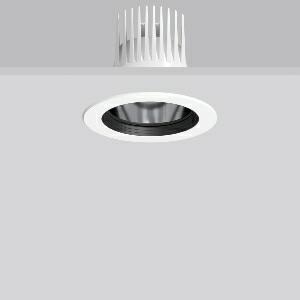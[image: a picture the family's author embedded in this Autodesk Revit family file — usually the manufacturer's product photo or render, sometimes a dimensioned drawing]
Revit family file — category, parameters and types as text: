
# Revit family: heledon_maxi_e_901759_002_2_76_2391
name_source: partatom
category: Lighting Fixtures
units: mm (PartAtom-declared; Revit-internal decimal feet)

## family parameters
Cut with Voids When Loaded = No
Host = Face
Light Source = No
Part Type = Normal
Room Calculation Point = No
Round Connector Dimension = Use Diameter
Shared = No

## types (1)
- HELEDON maxi E (1 x LED Modul 927, 3050 lm, 2700)
    Apparent Load = 25 VA
    Approval mark = CE
    CIE Flux Codes = 97 100 100 100 100
    Color Rendering = 92
    Color Temperature = 2700
    Default Elevation = 1800 mm
    Description = Series: HELEDON maxi
Round recessed downlight. Housing: die-cast aluminium, powder-coated. Black plastic ring and recessed LED to prevent glare from the side. Optical assembly with reflector made of MIRO-Silver with 98% total light reflection for outstanding efficiency - can be changed without tools. Best colour rendering index Ra>90. Suitable for Recessed ceiling mounting. Installation without tools thanks to spring fastening system. Including separate LED converter with connecting cable 600 mm.High quality converter without flickering and stroboscopic effect. Through-wiring box (5 pole) available as accessory. The following accessories can be mounted without use of tools: interchangeable lenses, decorative glasses, honeycomb louvre, clear and frosted diffusers, white interchangeable plastic ring. 
Colour: traffic white, matt (RAL 9016)
Diameter: 162 mm
Height: 3 mm
Cut-out diameter: 152 mm
Recess height: 200 mm
Luminaire: recess height: 135 mm
Lamp: LED
Socket: without socket
Colour temperature: 2700K
Colour rendering index (CRI): 92
System power: 25 W
Rated luminous flux: 3050 lm
Luminous efficiency: 122 lm/W
Control gear: Converter, dimmable, DALI
Protection class: II
Type of protection: IP 20
    Height = 0 mm  [stored 0 ft]
    Lamp = 1 x LED Modul 927
    Lamp Light Flux = 3050 lm
    Lamp count = 1
    Length = 162 mm
    Lifetime = 50000 h
    Luminous efficacy = 122 lm/W
    Manufacturer = RZB
    ModVariant = No
    Model = 901759.002.2.76
    Mounting Place = Ceiling
    Mounting Type = Recessed
    Number of Poles = 1
    OnlyDefault = Yes
    Power Factor = 1
    Product Name = HELEDON maxi E
    Product group = Recessed downlights
    ProductGroupID = 402
    Protection Class = Protection class II
    Protection Degree = IP 20
    RLX_Detail_Level = 1
    RLX_Emergency_Light_Flux = 0 lm
    RLX_Emergency_Type = 0
    RLX_Emergency_Type_DB = No
    RlxData = <blob elided: 119373 chars, md5=dc6d9304>
    Socket = socket
    Standby Power = 0 W
    System Light Flux = 3050 lm
    System Power = 25 W
    Type Comments = Product without accessories
    Type Image = 901662.002.jpg
    URL = http://relux.com
    VarID = ---
    Voltage = 230 V
    Voltage Range = 220-240 V
    Weight = 0.00 kg
    Width = 0 mm  [stored 0 ft]

note: [stored X ft] marks values corroborated as IEEE doubles in the binary element streams (Revit-internal decimal feet)

## geometry (parser evidence)
native form markers: Blend x4, Sweep x11
no freeform markers — native parametric forms only
